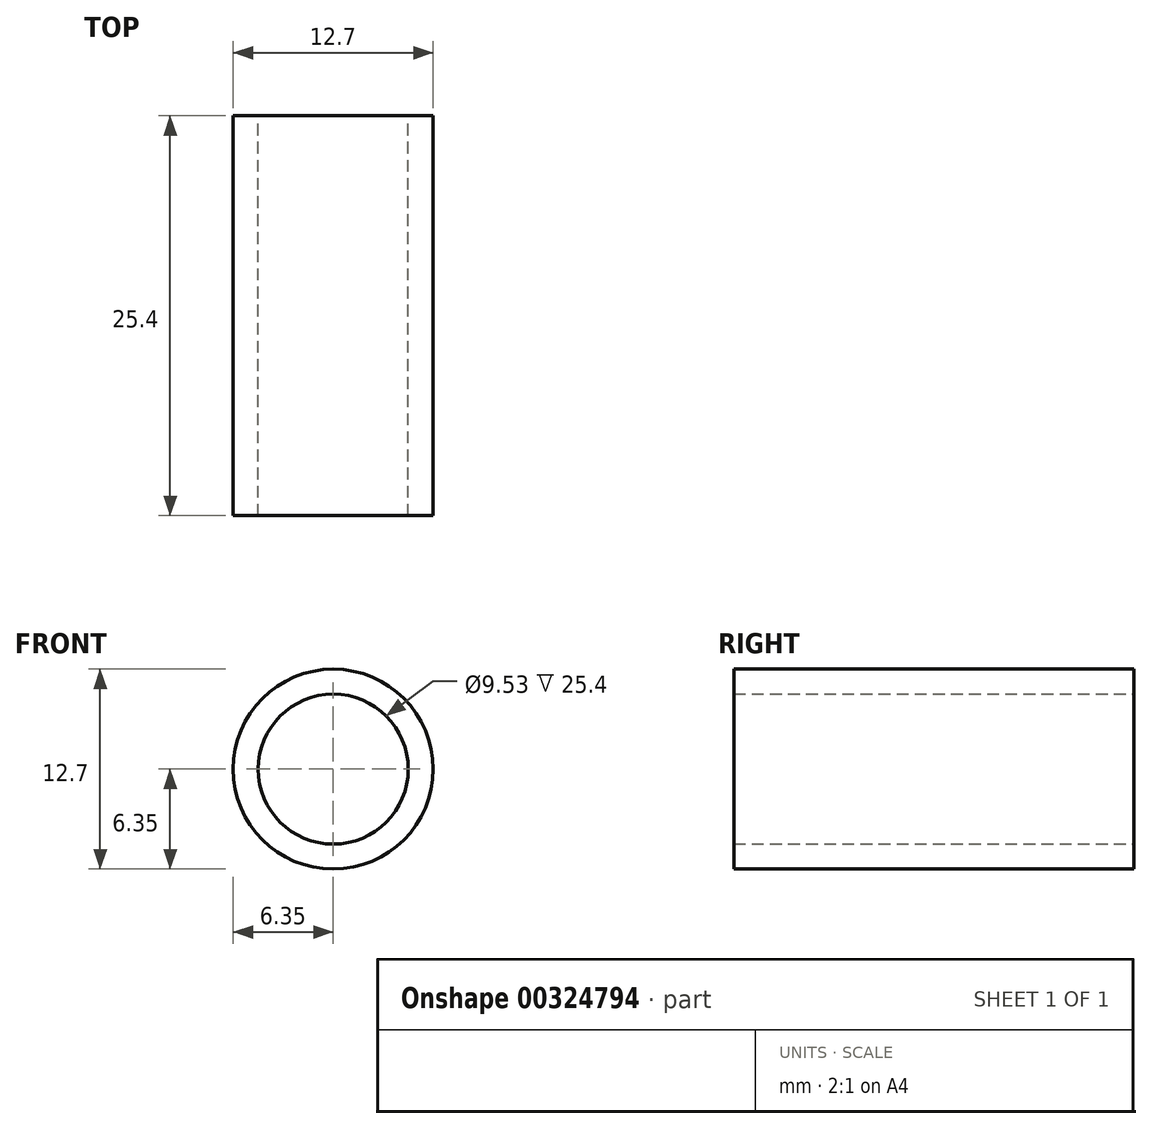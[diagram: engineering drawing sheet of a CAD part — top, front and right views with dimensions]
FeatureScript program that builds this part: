
annotation { "Feature Type Name" : "Feature", "Feature Type Description" : "" }
export const myFeature = defineFeature(function(context is Context, id is Id, definition is map)
    precondition{}
    {
        {
            var Q0;
            Q0=qCreatedBy(makeId("Front.planeOp"),FACE);
            var sketch = newSketch(context, id + "F0", { "sketchPlane" : qUnion([Q0])});
            skCircle(sketch, "E0", {"center": v(0, 0) * mm, "radius": 4.76 * mm});
            skCircle(sketch, "E1", {"center": v(0, 0) * mm, "radius": 6.35 * mm});
            skSolve(sketch);
        }
        {
            var Q0;
            Q0=makeQuery(id+"F0.imprint","IMPRINT",FACE,{"disambiguationData":[TD([[makeQuery(id+"F0.imprint","IMPRINT",EDGE,{"derivedFrom":sQuery(id+"F0.wireOp",EDGE,"E0")}),-1.0]])]});
            extrude(context, id + "F1", {"entities" : qUnion([Q0]), "depth" : 25.4 * mm, "offsetDistance" : 25.4 * mm});
        }
    });
